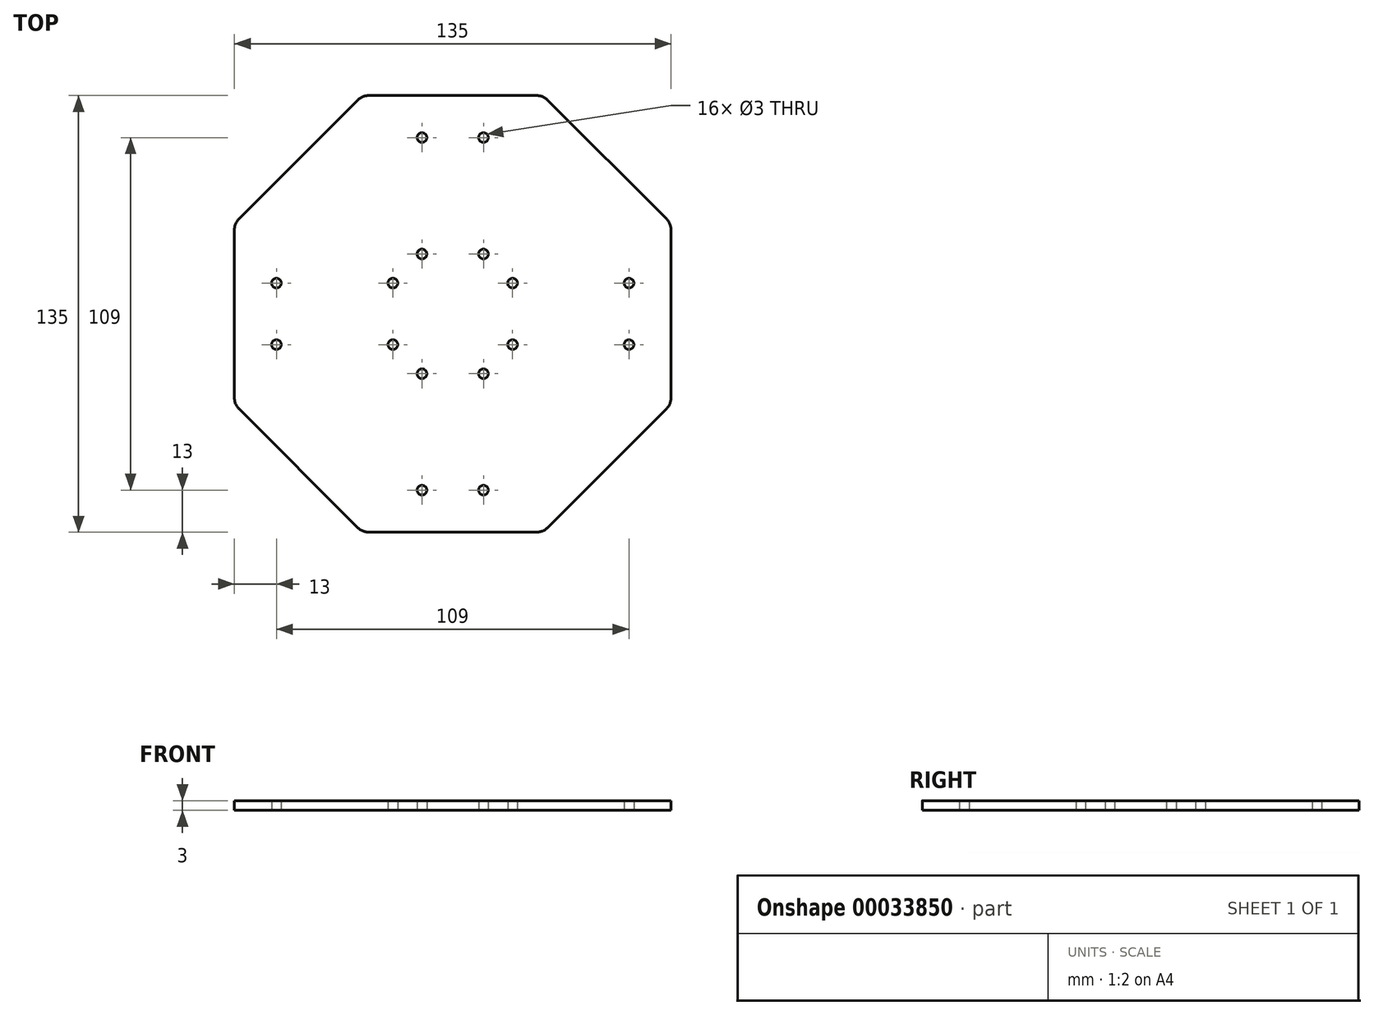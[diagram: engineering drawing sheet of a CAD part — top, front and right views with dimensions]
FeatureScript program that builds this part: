
annotation { "Feature Type Name" : "Feature", "Feature Type Description" : "" }
export const myFeature = defineFeature(function(context is Context, id is Id, definition is map)
    precondition{}
    {
        {
            var Q0;
            Q0=qCreatedBy(makeId("Top.planeOp"),FACE);
            var sketch = newSketch(context, id + "F0", { "sketchPlane" : qUnion([Q0])});
            skPoint(sketch, "E0.rect.middle", {"position": v(0, 0) * mm});
            skLineSegment(sketch, "E1", {"start": v(0, 67.5) * mm, "end": v(0, -67.5) * mm, "construction": true});
            skLineSegment(sketch, "E2", {"start": v(-67.5, 0) * mm, "end": v(67.5, 0) * mm, "construction": true});
            skLineSegment(sketch, "E3.rect.bottom", {"start": v(14, -14) * mm, "end": v(-14, -14) * mm, "construction": true});
            skLineSegment(sketch, "E3.rect.top", {"start": v(14, 14) * mm, "end": v(-14, 14) * mm, "construction": true});
            skLineSegment(sketch, "E3.rect.left", {"start": v(14, -14) * mm, "end": v(14, 14) * mm, "construction": true});
            skLineSegment(sketch, "E3.rect.right", {"start": v(-14, -14) * mm, "end": v(-14, 14) * mm, "construction": true});
            skLineSegment(sketch, "E4.rect.bottom", {"start": v(5, -5) * mm, "end": v(-5, -5) * mm, "construction": true});
            skLineSegment(sketch, "E4.rect.top", {"start": v(5, 5) * mm, "end": v(-5, 5) * mm, "construction": true});
            skLineSegment(sketch, "E4.rect.left", {"start": v(5, -5) * mm, "end": v(5, 5) * mm, "construction": true});
            skLineSegment(sketch, "E4.rect.right", {"start": v(-5, -5) * mm, "end": v(-5, 5) * mm, "construction": true});
            skLineSegment(sketch, "E5.bottom", {"start": v(-14, 14) * mm, "end": v(14, 14) * mm, "construction": true});
            skLineSegment(sketch, "E5.top", {"start": v(-14, 23) * mm, "end": v(14, 23) * mm, "construction": true});
            skLineSegment(sketch, "E5.left", {"start": v(-14, 14) * mm, "end": v(-14, 23) * mm, "construction": true});
            skLineSegment(sketch, "E5.right", {"start": v(14, 14) * mm, "end": v(14, 23) * mm, "construction": true});
            skLineSegment(sketch, "E6", {"start": v(5, 23) * mm, "end": v(5, 14) * mm, "construction": true});
            skLineSegment(sketch, "E7", {"start": v(14, 18.5) * mm, "end": v(5, 18.5) * mm, "construction": true});
            skCircle(sketch, "E8", {"center": v(9.5, 18.5) * mm, "radius": 1.5 * mm});
            skCircle(sketch, "E9.MirrorC", {"center": v(-9.5, 18.5) * mm, "radius": 1.5 * mm});
            skCircle(sketch, "E10.MirrorC", {"center": v(-9.5, -18.5) * mm, "radius": 1.5 * mm});
            skCircle(sketch, "E11.MirrorC", {"center": v(9.5, -18.5) * mm, "radius": 1.5 * mm});
            skCircle(sketch, "E12", {"center": v(0, 0) * mm, "radius": 20.8 * mm, "construction": true});
            skLineSegment(sketch, "E13", {"start": v(0, 0) * mm, "end": v(14, 14) * mm, "construction": true});
            skCircle(sketch, "E14.MirrorC", {"center": v(18.5, -9.5) * mm, "radius": 1.5 * mm});
            skCircle(sketch, "E15.MirrorC", {"center": v(18.5, 9.5) * mm, "radius": 1.5 * mm});
            skLineSegment(sketch, "E16", {"start": v(0, 0) * mm, "end": v(-14, 14) * mm, "construction": true});
            skCircle(sketch, "E17.MirrorC", {"center": v(-18.5, 9.5) * mm, "radius": 1.5 * mm});
            skCircle(sketch, "E18.MirrorC", {"center": v(-18.5, -9.5) * mm, "radius": 1.5 * mm});
            skCircle(sketch, "E19", {"center": v(9.5, 54.5) * mm, "radius": 1.5 * mm});
            skCircle(sketch, "E20.MirrorC", {"center": v(-9.5, 54.5) * mm, "radius": 1.5 * mm});
            skCircle(sketch, "E21.MirrorC", {"center": v(-9.5, -54.5) * mm, "radius": 1.5 * mm});
            skCircle(sketch, "E22.MirrorC", {"center": v(9.5, -54.5) * mm, "radius": 1.5 * mm});
            skCircle(sketch, "E23.MirrorC", {"center": v(54.5, -9.5) * mm, "radius": 1.5 * mm});
            skCircle(sketch, "E24.MirrorC", {"center": v(54.5, 9.5) * mm, "radius": 1.5 * mm});
            skCircle(sketch, "E25.MirrorC", {"center": v(-54.5, -9.5) * mm, "radius": 1.5 * mm});
            skCircle(sketch, "E26.MirrorC", {"center": v(-54.5, 9.5) * mm, "radius": 1.5 * mm});
            skLineSegment(sketch, "E27", {"start": v(0, 0) * mm, "end": v(95.46, 0) * mm, "construction": true});
            skLineSegment(sketch, "E28.MirrorCS", {"start": v(0, 0) * mm, "end": v(0, 95.46) * mm, "construction": true});
            skLineSegment(sketch, "E29", {"start": v(27.96, 67.5) * mm, "end": v(67.5, 27.96) * mm});
            skLineSegment(sketch, "E30.MirrorCS", {"start": v(-67.5, -27.96) * mm, "end": v(-27.96, -67.5) * mm});
            skLineSegment(sketch, "E31.MirrorCS", {"start": v(-27.96, 67.5) * mm, "end": v(-67.5, 27.96) * mm});
            skLineSegment(sketch, "E32.MirrorCS", {"start": v(27.96, -67.5) * mm, "end": v(67.5, -27.96) * mm});
            skLineSegment(sketch, "E33", {"start": v(67.5, -27.96) * mm, "end": v(67.5, 27.96) * mm});
            skLineSegment(sketch, "E34.MirrorCS", {"start": v(-67.5, -27.96) * mm, "end": v(-67.5, 27.96) * mm});
            skLineSegment(sketch, "E35.MirrorCS", {"start": v(-27.96, 67.5) * mm, "end": v(27.96, 67.5) * mm});
            skLineSegment(sketch, "E36.MirrorCS", {"start": v(27.96, -67.5) * mm, "end": v(-27.96, -67.5) * mm});
            skPoint(sketch, "E37.orphan", {"position": v(0, 95.46) * mm});
            skPoint(sketch, "E38.orphan", {"position": v(95.46, 0) * mm});
            skPoint(sketch, "E39.orphan", {"position": v(0, -95.46) * mm});
            skPoint(sketch, "E40.orphan", {"position": v(-95.46, 0) * mm});
            skSolve(sketch);
        }
        {
            var Q0;
            Q0=qSketchRegion(id+"F0",true);
            extrude(context, id + "F1", {"entities" : qUnion([Q0]), "depth" : 3 * mm});
        }
        {
            var Q0;
            Q0=makeQuery(id+"F1.opExtrude","SWEPT_EDGE",EDGE,{"disambiguationData":[OSD([sQuery(id+"F0.wireOp",EDGE,"E31.MirrorCS"),sQuery(id+"F0.wireOp",EDGE,"E35.MirrorCS")])]});
            var Q1;
            Q1=makeQuery(id+"F1.opExtrude","SWEPT_EDGE",EDGE,{"disambiguationData":[OSD([sQuery(id+"F0.wireOp",EDGE,"E31.MirrorCS"),sQuery(id+"F0.wireOp",EDGE,"E34.MirrorCS")])]});
            var Q2;
            Q2=makeQuery(id+"F1.opExtrude","SWEPT_EDGE",EDGE,{"disambiguationData":[OSD([sQuery(id+"F0.wireOp",EDGE,"E30.MirrorCS"),sQuery(id+"F0.wireOp",EDGE,"E34.MirrorCS")])]});
            var Q3;
            Q3=makeQuery(id+"F1.opExtrude","SWEPT_EDGE",EDGE,{"disambiguationData":[OSD([sQuery(id+"F0.wireOp",EDGE,"E30.MirrorCS"),sQuery(id+"F0.wireOp",EDGE,"E36.MirrorCS")])]});
            var Q4;
            Q4=makeQuery(id+"F1.opExtrude","SWEPT_EDGE",EDGE,{"disambiguationData":[OSD([sQuery(id+"F0.wireOp",EDGE,"E32.MirrorCS"),sQuery(id+"F0.wireOp",EDGE,"E36.MirrorCS")])]});
            var Q5;
            Q5=makeQuery(id+"F1.opExtrude","SWEPT_EDGE",EDGE,{"disambiguationData":[OSD([sQuery(id+"F0.wireOp",EDGE,"E32.MirrorCS"),sQuery(id+"F0.wireOp",EDGE,"E33")])]});
            var Q6;
            Q6=makeQuery(id+"F1.opExtrude","SWEPT_EDGE",EDGE,{"disambiguationData":[OSD([sQuery(id+"F0.wireOp",EDGE,"E29"),sQuery(id+"F0.wireOp",EDGE,"E33")])]});
            var Q7;
            Q7=makeQuery(id+"F1.opExtrude","SWEPT_EDGE",EDGE,{"disambiguationData":[OSD([sQuery(id+"F0.wireOp",EDGE,"E29"),sQuery(id+"F0.wireOp",EDGE,"E35.MirrorCS")])]});
            fillet(context, id + "F2", {"entities" : qUnion([Q0, Q1, Q2, Q3, Q4, Q5, Q6, Q7]), "radius" : 5 * mm, "tangentPropagation" : true, "allowEdgeOverflow" : false});
        }
    });
